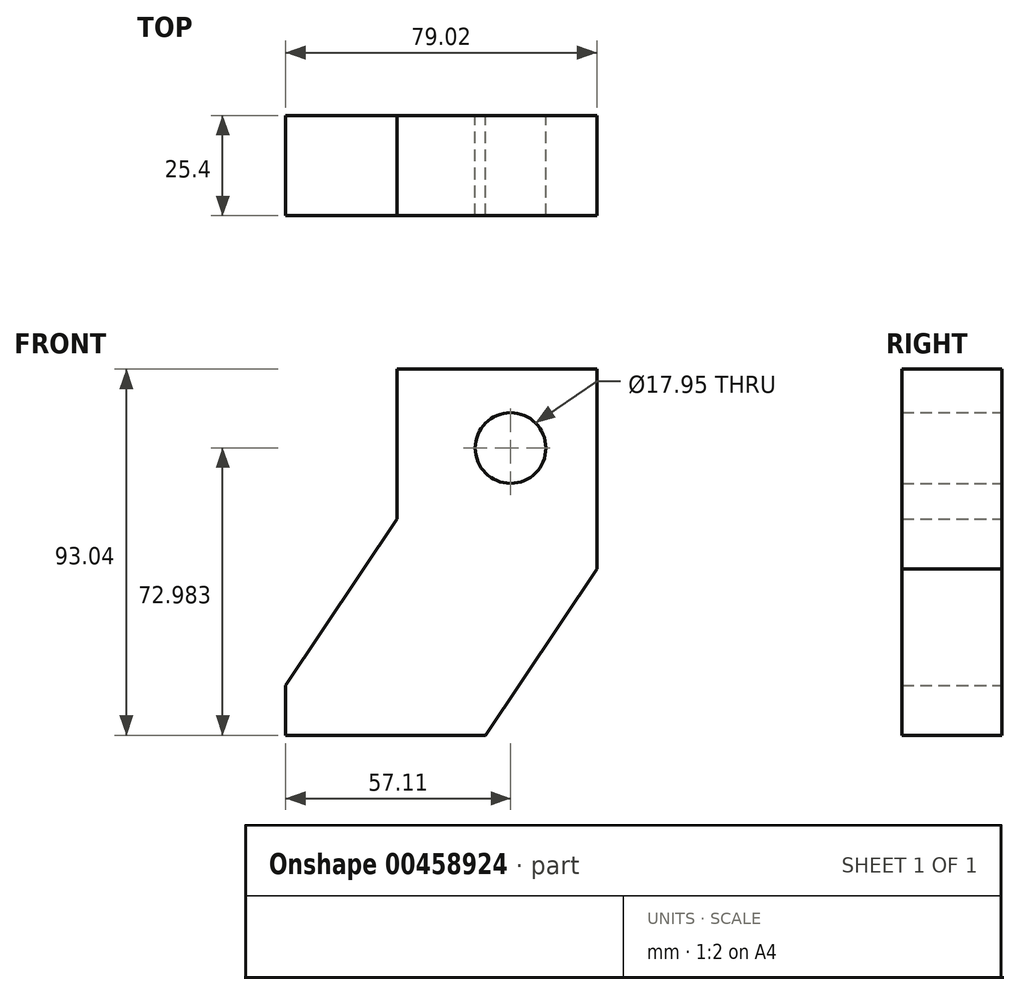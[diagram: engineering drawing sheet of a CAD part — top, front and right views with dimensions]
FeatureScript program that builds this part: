
annotation { "Feature Type Name" : "Feature", "Feature Type Description" : "" }
export const myFeature = defineFeature(function(context is Context, id is Id, definition is map)
    precondition{}
    {
        {
            var Q0;
            Q0=qCreatedBy(makeId("Front.planeOp"),FACE);
            var sketch = newSketch(context, id + "F0", { "sketchPlane" : qUnion([Q0])});
            skLineSegment(sketch, "E0.bottom", {"start": v(-57.1, -32.06) * mm, "end": v(-6.3, -32.06) * mm});
            skLineSegment(sketch, "E0.top", {"start": v(-57.1, -44.76) * mm, "end": v(-6.3, -44.76) * mm});
            skLineSegment(sketch, "E0.left", {"start": v(-57.1, -32.06) * mm, "end": v(-57.1, -44.76) * mm});
            skLineSegment(sketch, "E0.right", {"start": v(-6.3, -32.06) * mm, "end": v(-6.3, -44.76) * mm});
            skLineSegment(sketch, "E1", {"start": v(-6.3, -32.06) * mm, "end": v(21.91, 10.18) * mm});
            skLineSegment(sketch, "E2", {"start": v(-28.89, 10.18) * mm, "end": v(-57.1, -32.06) * mm});
            skLineSegment(sketch, "E3", {"start": v(-6.3, -44.76) * mm, "end": v(21.91, -2.52) * mm});
            skLineSegment(sketch, "E4", {"start": v(21.91, -2.52) * mm, "end": v(21.91, 10.18) * mm});
            skLineSegment(sketch, "E5", {"start": v(-28.89, -2.52) * mm, "end": v(-28.89, 10.18) * mm});
            skLineSegment(sketch, "E6", {"start": v(21.91, -2.52) * mm, "end": v(-28.89, -2.52) * mm});
            skLineSegment(sketch, "E7", {"start": v(-28.89, -2.52) * mm, "end": v(-57.1, -44.76) * mm});
            skLineSegment(sketch, "E8", {"start": v(-28.89, 10.18) * mm, "end": v(21.91, 10.18) * mm});
            skLineSegment(sketch, "E9", {"start": v(-28.89, 10.18) * mm, "end": v(-28.89, 48.28) * mm});
            skLineSegment(sketch, "E10", {"start": v(-28.89, 48.28) * mm, "end": v(21.91, 48.28) * mm});
            skLineSegment(sketch, "E11", {"start": v(21.91, 48.28) * mm, "end": v(21.91, 10.18) * mm});
            skCircle(sketch, "E12", {"center": v(0, 28.22) * mm, "radius": 8.98 * mm});
            skSolve(sketch);
        }
        {
            var Q0;
            Q0 = qSketchRegion(id + "F0", true);
            var Q1;
            {var subQ1=sQuery(id+"F0.wireOp",EDGE,"E0.bottom");var subQ3=sQuery(id+"F0.wireOp",EDGE,"E7");var subQ4=makeQuery(id+"F0.imprint","INTERSECT",VERTEX,{"derivedFrom":[subQ1,subQ3]});Q1=makeQuery(id+"F0.imprint","IMPRINT",FACE,{"disambiguationData":[TD([[makeQuery(id+"F0.imprint","IMPRINT",EDGE,{"disambiguationData":[TD([[subQ4,-1.0]])],"derivedFrom":subQ1}),1.0]])]});}
            extrude(context, id + "F1", {"entities" : qUnion([Q0, Q1]), "depth" : 25.4 * mm});
        }
    });
